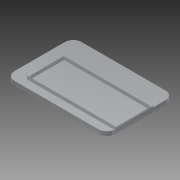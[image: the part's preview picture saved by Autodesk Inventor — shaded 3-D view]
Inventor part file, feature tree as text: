
AUTODESK INVENTOR PART (.ipt)
format: ipt  version: 2014 (Build 180170000, 170)  size: 133,120 bytes
history: native  units: mm
features: reference x12, extrude x2, sketch x2
ambient origin geometry x8: Origin, YZ Plane, XZ Plane, XY Plane, X Axis, Y Axis, Z Axis, Center Point
bodies: Solid1 (feature_tree)
feature tree (16):
  extrude  "Extrusion1"  Depth=51.0mm
  extrude  "Extrusion2"  Depth=53.0mm
  sketch  "Sketch1"  dims[d0=2.5mm d1=0.0mm d2=51.0mm]
  reference  "Reference1"
  reference  "Reference2"
  reference  "Reference3"
  reference  "Reference4"
  reference  "Reference5"
  reference  "Reference6"
  reference  "Reference7"
  reference  "Reference8"
  reference  "Reference9"
  reference  "Reference10"
  reference  "Reference11"
  reference  "Reference12"
  sketch  "Sketch2"  dims[d3=20.0mm d4=53.0mm d5=22.0mm d6=2.0mm d7=0.0mm]
